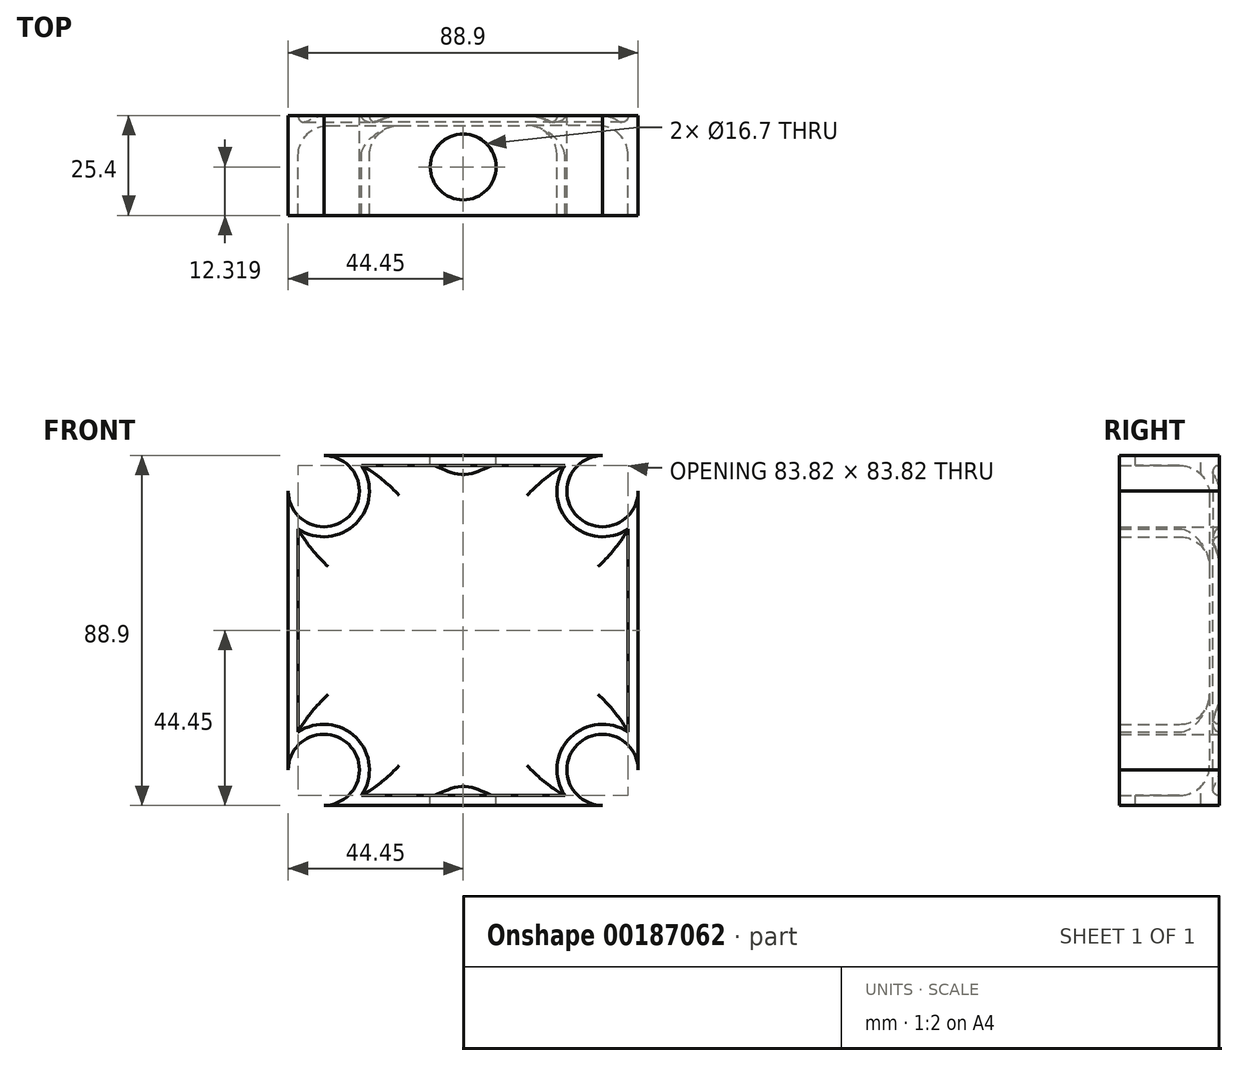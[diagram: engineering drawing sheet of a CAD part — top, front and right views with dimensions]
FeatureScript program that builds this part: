
annotation { "Feature Type Name" : "Feature", "Feature Type Description" : "" }
export const myFeature = defineFeature(function(context is Context, id is Id, definition is map)
    precondition{}
    {
        {
            var Q0;
            Q0=qCreatedBy(makeId("Front.planeOp"),FACE);
            var sketch = newSketch(context, id + "F0", { "sketchPlane" : qUnion([Q0])});
            skLineSegment(sketch, "E0.bottom", {"start": v(-35.4, 44.45) * mm, "end": v(35.4, 44.45) * mm});
            skLineSegment(sketch, "E0.top", {"start": v(-35.4, -44.45) * mm, "end": v(35.4, -44.45) * mm});
            skLineSegment(sketch, "E0.left", {"start": v(-44.45, 35.4) * mm, "end": v(-44.45, -35.4) * mm});
            skLineSegment(sketch, "E0.right", {"start": v(44.45, 35.4) * mm, "end": v(44.45, -35.4) * mm});
            skLineSegment(sketch, "E1", {"start": v(0, 75.45) * mm, "end": v(0, -69.09) * mm, "construction": true});
            skLineSegment(sketch, "E2", {"start": v(-67.75, 0) * mm, "end": v(74.89, 0) * mm, "construction": true});
            skArc(sketch, "E3", {"start": v(-44.45, 35.4) * mm, "mid": v(-29, 29) * mm, "end": v(-35.4, 44.45) * mm});
            skArc(sketch, "E4.MirrorC", {"start": v(44.45, 35.4) * mm, "mid": v(29, 29) * mm, "end": v(35.4, 44.45) * mm});
            skArc(sketch, "E5.MirrorC", {"start": v(44.45, -35.4) * mm, "mid": v(29, -29) * mm, "end": v(35.4, -44.45) * mm});
            skArc(sketch, "E6.MirrorC", {"start": v(-44.45, -35.4) * mm, "mid": v(-29, -29) * mm, "end": v(-35.4, -44.45) * mm});
            skPoint(sketch, "E7.orphan", {"position": v(-44.45, 44.45) * mm});
            skSolve(sketch);
        }
        {
            var Q0;
            Q0 = qSketchRegion(id + "F0", true);
            extrude(context, id + "F1", {"entities" : qUnion([Q0]), "depth" : 25.4 * mm});
        }
        {
            var Q0;
            Q0=makeQuery(id+"F1.opExtrude","CAP_FACE",FACE,{"disambiguationData":[OSD([sQuery(id+"F0.wireOp",EDGE,"E0.bottom"),sQuery(id+"F0.wireOp",EDGE,"E0.top"),sQuery(id+"F0.wireOp",EDGE,"E0.left"),sQuery(id+"F0.wireOp",EDGE,"E0.right"),sQuery(id+"F0.wireOp",EDGE,"E3"),sQuery(id+"F0.wireOp",EDGE,"E4.MirrorC"),sQuery(id+"F0.wireOp",EDGE,"E5.MirrorC"),sQuery(id+"F0.wireOp",EDGE,"E6.MirrorC")])],"isStart":false});
            shell(context, id + "F2", {"entities" : qUnion([Q0]), "thickness" : 2.54 * mm});
        }
        {
            var Q0;
            {var subQ0=sQuery(id+"F0.wireOp",EDGE,"E0.right");Q0=makeQuery(id+"F2.opShell","OFFSET_EDGE",EDGE,{"disambiguationData":[OSD([subQ0]),TDD([makeQuery(id+"F1.opExtrude","CAP_EDGE",EDGE,{"disambiguationData":[OSD([subQ0])],"isStart":true})])]});}
            var Q1;
            {var subQ0=sQuery(id+"F0.wireOp",EDGE,"E4.MirrorC");Q1=makeQuery(id+"F2.opShell","OFFSET_EDGE",EDGE,{"disambiguationData":[OSD([subQ0]),TDD([makeQuery(id+"F1.opExtrude","CAP_EDGE",EDGE,{"disambiguationData":[OSD([subQ0])],"isStart":true})])]});}
            var Q2;
            {var subQ0=sQuery(id+"F0.wireOp",EDGE,"E0.bottom");Q2=makeQuery(id+"F2.opShell","OFFSET_EDGE",EDGE,{"disambiguationData":[OSD([subQ0]),TDD([makeQuery(id+"F1.opExtrude","CAP_EDGE",EDGE,{"disambiguationData":[OSD([subQ0])],"isStart":true})])]});}
            var Q3;
            {var subQ0=sQuery(id+"F0.wireOp",EDGE,"E3");Q3=makeQuery(id+"F2.opShell","OFFSET_EDGE",EDGE,{"disambiguationData":[OSD([subQ0]),TDD([makeQuery(id+"F1.opExtrude","CAP_EDGE",EDGE,{"disambiguationData":[OSD([subQ0])],"isStart":true})])]});}
            var Q4;
            {var subQ0=sQuery(id+"F0.wireOp",EDGE,"E0.left");Q4=makeQuery(id+"F2.opShell","OFFSET_EDGE",EDGE,{"disambiguationData":[OSD([subQ0]),TDD([makeQuery(id+"F1.opExtrude","CAP_EDGE",EDGE,{"disambiguationData":[OSD([subQ0])],"isStart":true})])]});}
            var Q5;
            {var subQ0=sQuery(id+"F0.wireOp",EDGE,"E6.MirrorC");Q5=makeQuery(id+"F2.opShell","OFFSET_EDGE",EDGE,{"disambiguationData":[OSD([subQ0]),TDD([makeQuery(id+"F1.opExtrude","CAP_EDGE",EDGE,{"disambiguationData":[OSD([subQ0])],"isStart":true})])]});}
            var Q6;
            {var subQ0=sQuery(id+"F0.wireOp",EDGE,"E0.top");Q6=makeQuery(id+"F2.opShell","OFFSET_EDGE",EDGE,{"disambiguationData":[OSD([subQ0]),TDD([makeQuery(id+"F1.opExtrude","CAP_EDGE",EDGE,{"disambiguationData":[OSD([subQ0])],"isStart":true})])]});}
            var Q7;
            {var subQ0=sQuery(id+"F0.wireOp",EDGE,"E5.MirrorC");Q7=makeQuery(id+"F2.opShell","OFFSET_EDGE",EDGE,{"disambiguationData":[OSD([subQ0]),TDD([makeQuery(id+"F1.opExtrude","CAP_EDGE",EDGE,{"disambiguationData":[OSD([subQ0])],"isStart":true})])]});}
            fillet(context, id + "F3", {"entities" : qUnion([Q0, Q1, Q2, Q3, Q4, Q5, Q6, Q7]), "radius" : 7.62 * mm, "tangentPropagation" : true, "allowEdgeOverflow" : false});
        }
        {
            var Q0;
            Q0=makeQuery(id+"F1.opExtrude","CAP_FACE",FACE,{"disambiguationData":[OSD([sQuery(id+"F0.wireOp",EDGE,"E0.bottom"),sQuery(id+"F0.wireOp",EDGE,"E0.top"),sQuery(id+"F0.wireOp",EDGE,"E0.left"),sQuery(id+"F0.wireOp",EDGE,"E0.right"),sQuery(id+"F0.wireOp",EDGE,"E3"),sQuery(id+"F0.wireOp",EDGE,"E4.MirrorC"),sQuery(id+"F0.wireOp",EDGE,"E5.MirrorC"),sQuery(id+"F0.wireOp",EDGE,"E6.MirrorC")])],"isStart":true});
            shell(context, id + "F4", {"entities" : qUnion([Q0]), "thickness" : 2.54 * mm});
        }
        {
            var Q0;
            {var subQ0=sQuery(id+"F0.wireOp",EDGE,"E0.right");Q0=makeQuery(id+"F4.opShell","TWEAK_EDGE",EDGE,{"derivedFrom":[makeQuery(id+"F1.opExtrude","SWEPT_FACE",FACE,{"disambiguationData":[OSD([subQ0])]}),makeQuery(id+"F3.opFillet","BLEND_FACE",FACE,{"disambiguationData":[OSD([subQ0])]})]});}
            var Q1;
            {var subQ0=sQuery(id+"F0.wireOp",EDGE,"E5.MirrorC");Q1=makeQuery(id+"F4.opShell","TWEAK_EDGE",EDGE,{"derivedFrom":[makeQuery(id+"F1.opExtrude","SWEPT_FACE",FACE,{"disambiguationData":[OSD([subQ0])]}),makeQuery(id+"F3.opFillet","BLEND_FACE",FACE,{"disambiguationData":[OSD([subQ0])]})]});}
            var Q2;
            {var subQ0=sQuery(id+"F0.wireOp",EDGE,"E0.top");Q2=makeQuery(id+"F4.opShell","TWEAK_EDGE",EDGE,{"derivedFrom":[makeQuery(id+"F1.opExtrude","SWEPT_FACE",FACE,{"disambiguationData":[OSD([subQ0])]}),makeQuery(id+"F3.opFillet","BLEND_FACE",FACE,{"disambiguationData":[OSD([subQ0])]})]});}
            var Q3;
            {var subQ0=sQuery(id+"F0.wireOp",EDGE,"E6.MirrorC");Q3=makeQuery(id+"F4.opShell","TWEAK_EDGE",EDGE,{"derivedFrom":[makeQuery(id+"F1.opExtrude","SWEPT_FACE",FACE,{"disambiguationData":[OSD([subQ0])]}),makeQuery(id+"F3.opFillet","BLEND_FACE",FACE,{"disambiguationData":[OSD([subQ0])]})]});}
            var Q4;
            {var subQ0=sQuery(id+"F0.wireOp",EDGE,"E0.left");Q4=makeQuery(id+"F4.opShell","TWEAK_EDGE",EDGE,{"derivedFrom":[makeQuery(id+"F1.opExtrude","SWEPT_FACE",FACE,{"disambiguationData":[OSD([subQ0])]}),makeQuery(id+"F3.opFillet","BLEND_FACE",FACE,{"disambiguationData":[OSD([subQ0])]})]});}
            var Q5;
            {var subQ0=sQuery(id+"F0.wireOp",EDGE,"E3");Q5=makeQuery(id+"F4.opShell","TWEAK_EDGE",EDGE,{"derivedFrom":[makeQuery(id+"F1.opExtrude","SWEPT_FACE",FACE,{"disambiguationData":[OSD([subQ0])]}),makeQuery(id+"F3.opFillet","BLEND_FACE",FACE,{"disambiguationData":[OSD([subQ0])]})]});}
            var Q6;
            {var subQ0=sQuery(id+"F0.wireOp",EDGE,"E0.bottom");Q6=makeQuery(id+"F4.opShell","TWEAK_EDGE",EDGE,{"derivedFrom":[makeQuery(id+"F1.opExtrude","SWEPT_FACE",FACE,{"disambiguationData":[OSD([subQ0])]}),makeQuery(id+"F3.opFillet","BLEND_FACE",FACE,{"disambiguationData":[OSD([subQ0])]})]});}
            var Q7;
            {var subQ0=sQuery(id+"F0.wireOp",EDGE,"E4.MirrorC");Q7=makeQuery(id+"F4.opShell","TWEAK_EDGE",EDGE,{"derivedFrom":[makeQuery(id+"F1.opExtrude","SWEPT_FACE",FACE,{"disambiguationData":[OSD([subQ0])]}),makeQuery(id+"F3.opFillet","BLEND_FACE",FACE,{"disambiguationData":[OSD([subQ0])]})]});}
            fillet(context, id + "F5", {"entities" : qUnion([Q0, Q1, Q2, Q3, Q4, Q5, Q6, Q7]), "radius" : 1.52 * mm, "tangentPropagation" : true, "allowEdgeOverflow" : false});
        }
        {
            var Q0;
            Q0=makeQuery(id+"F1.opExtrude","SWEPT_FACE",FACE,{"disambiguationData":[OSD([sQuery(id+"F0.wireOp",EDGE,"E0.bottom")])]});
            var sketch = newSketch(context, id + "F7", { "sketchPlane" : qUnion([Q0])});
            skCircle(sketch, "E8", {"center": v(0, -13.08) * mm, "radius": 8.35 * mm});
            skSolve(sketch);
        }
        {
            var Q0;
            Q0 = qSketchRegion(id + "F7", true);
            extrude(context, id + "F6", {"entities" : qUnion([Q0]), "operationType" : NewBodyOperationType.REMOVE, "oppositeDirection" : true, "depth" : 109.9 * mm});
        }
    });
